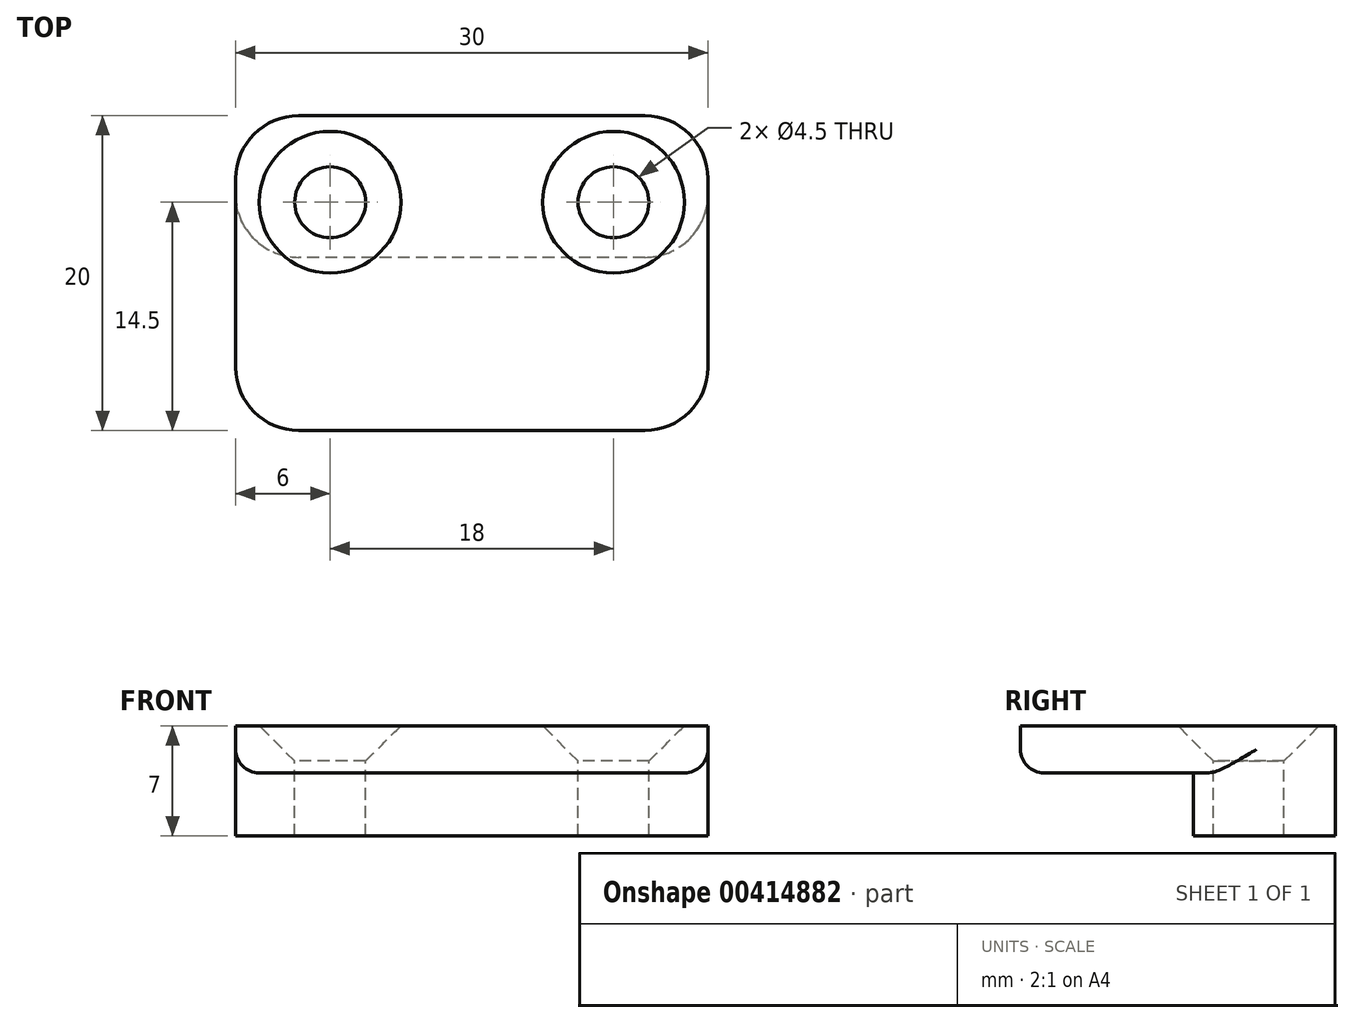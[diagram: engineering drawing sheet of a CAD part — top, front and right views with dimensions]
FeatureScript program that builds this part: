
annotation { "Feature Type Name" : "Feature", "Feature Type Description" : "" }
export const myFeature = defineFeature(function(context is Context, id is Id, definition is map)
    precondition{}
    {
        {
            var Q0;
            Q0=qCreatedBy(makeId("Right.planeOp"),FACE);
            var sketch = newSketch(context, id + "F0", { "sketchPlane" : qUnion([Q0])});
            skLineSegment(sketch, "E0", {"start": v(0, 0) * mm, "end": v(0, 4) * mm});
            skLineSegment(sketch, "E1", {"start": v(0, 4) * mm, "end": v(-11, 4) * mm});
            skLineSegment(sketch, "E2", {"start": v(-11, 4) * mm, "end": v(-11, 7) * mm});
            skLineSegment(sketch, "E3", {"start": v(-11, 7) * mm, "end": v(9, 7) * mm});
            skLineSegment(sketch, "E4", {"start": v(9, 7) * mm, "end": v(9, 0) * mm});
            skLineSegment(sketch, "E5", {"start": v(9, 0) * mm, "end": v(0, 0) * mm});
            skSolve(sketch);
        }
        {
            var Q0;
            Q0=makeQuery(id+"F0.imprint","IMPRINT",FACE,{"disambiguationData":[TD([[makeQuery(id+"F0.imprint","IMPRINT",EDGE,{"derivedFrom":sQuery(id+"F0.wireOp",EDGE,"E0")}),-1.0]])]});
            extrude(context, id + "F1", {"entities" : qUnion([Q0]), "endBound" : BoundingType.SYMMETRIC, "depth" : 30 * mm});
        }
        {
            var Q0;
            Q0=makeQuery(id+"F1.opExtrude","SWEPT_FACE",FACE,{"disambiguationData":[OSD([sQuery(id+"F0.wireOp",EDGE,"E3")])]});
            var sketch = newSketch(context, id + "F2", { "sketchPlane" : qUnion([Q0])});
            skLineSegment(sketch, "E6", {"start": v(-9, 3.5) * mm, "end": v(9, 3.5) * mm, "construction": true});
            skPoint(sketch, "E7.0", {"position": v(0, -11) * mm});
            skLineSegment(sketch, "E8", {"start": v(0, -11) * mm, "end": v(0, 3.5) * mm, "construction": true});
            skSolve(sketch);
        }
        {
            var Q0;
            Q0=sQuery(id+"F2.wireOp",VERTEX,"E6.start");
            var Q1;
            Q1=sQuery(id+"F2.wireOp",VERTEX,"E6.end");
            var Q2;
            Q2=makeQuery(id+"F1.opExtrude","SWEPT_BODY",BODY,{"disambiguationData":[OSD([sQuery(id+"F0.wireOp",EDGE,"E0"),sQuery(id+"F0.wireOp",EDGE,"E1"),sQuery(id+"F0.wireOp",EDGE,"E2"),sQuery(id+"F0.wireOp",EDGE,"E3"),sQuery(id+"F0.wireOp",EDGE,"E4"),sQuery(id+"F0.wireOp",EDGE,"E5")])]});
            hole(context, id + "F3", {"style" : HoleStyle.C_SINK, "endStyle" : HoleEndStyle.THROUGH, "holeDiameter" : 4.5 * mm, "cSinkDiameter" : 9 * mm, "cSinkAngle" : 90 * degree, "isTappedThrough" : true, "tappedDepth" : 12 * mm, "tapClearance" : 3, "locations" : qUnion([Q0, Q1]), "scope" : qUnion([Q2])});
        }
        {
            var Q0;
            Q0=makeQuery(id+"F1.opExtrude","CAP_EDGE",EDGE,{"disambiguationData":[OSD([sQuery(id+"F0.wireOp",EDGE,"E2")])],"isStart":false});
            var Q1;
            Q1=makeQuery(id+"F1.opExtrude","CAP_EDGE",EDGE,{"disambiguationData":[OSD([sQuery(id+"F0.wireOp",EDGE,"E2")])],"isStart":true});
            var Q2;
            Q2=makeQuery(id+"F1.opExtrude","CAP_EDGE",EDGE,{"disambiguationData":[OSD([sQuery(id+"F0.wireOp",EDGE,"E0")])],"isStart":false});
            var Q3;
            Q3=makeQuery(id+"F1.opExtrude","CAP_EDGE",EDGE,{"disambiguationData":[OSD([sQuery(id+"F0.wireOp",EDGE,"E0")])],"isStart":true});
            var Q4;
            Q4=makeQuery(id+"F1.opExtrude","CAP_EDGE",EDGE,{"disambiguationData":[OSD([sQuery(id+"F0.wireOp",EDGE,"E4")])],"isStart":true});
            var Q5;
            Q5=makeQuery(id+"F1.opExtrude","CAP_EDGE",EDGE,{"disambiguationData":[OSD([sQuery(id+"F0.wireOp",EDGE,"E4")])],"isStart":false});
            fillet(context, id + "F4", {"entities" : qUnion([Q0, Q1, Q2, Q3, Q4, Q5]), "radius" : 4 * mm, "tangentPropagation" : true, "allowEdgeOverflow" : false});
        }
        {
            var Q0;
            Q0=makeQuery(id+"F1.opExtrude","CAP_EDGE",EDGE,{"disambiguationData":[OSD([sQuery(id+"F0.wireOp",EDGE,"E1")])],"isStart":true});
            fillet(context, id + "F5", {"entities" : qUnion([Q0]), "radius" : 1.5 * mm, "tangentPropagation" : true, "allowEdgeOverflow" : false});
        }
    });
